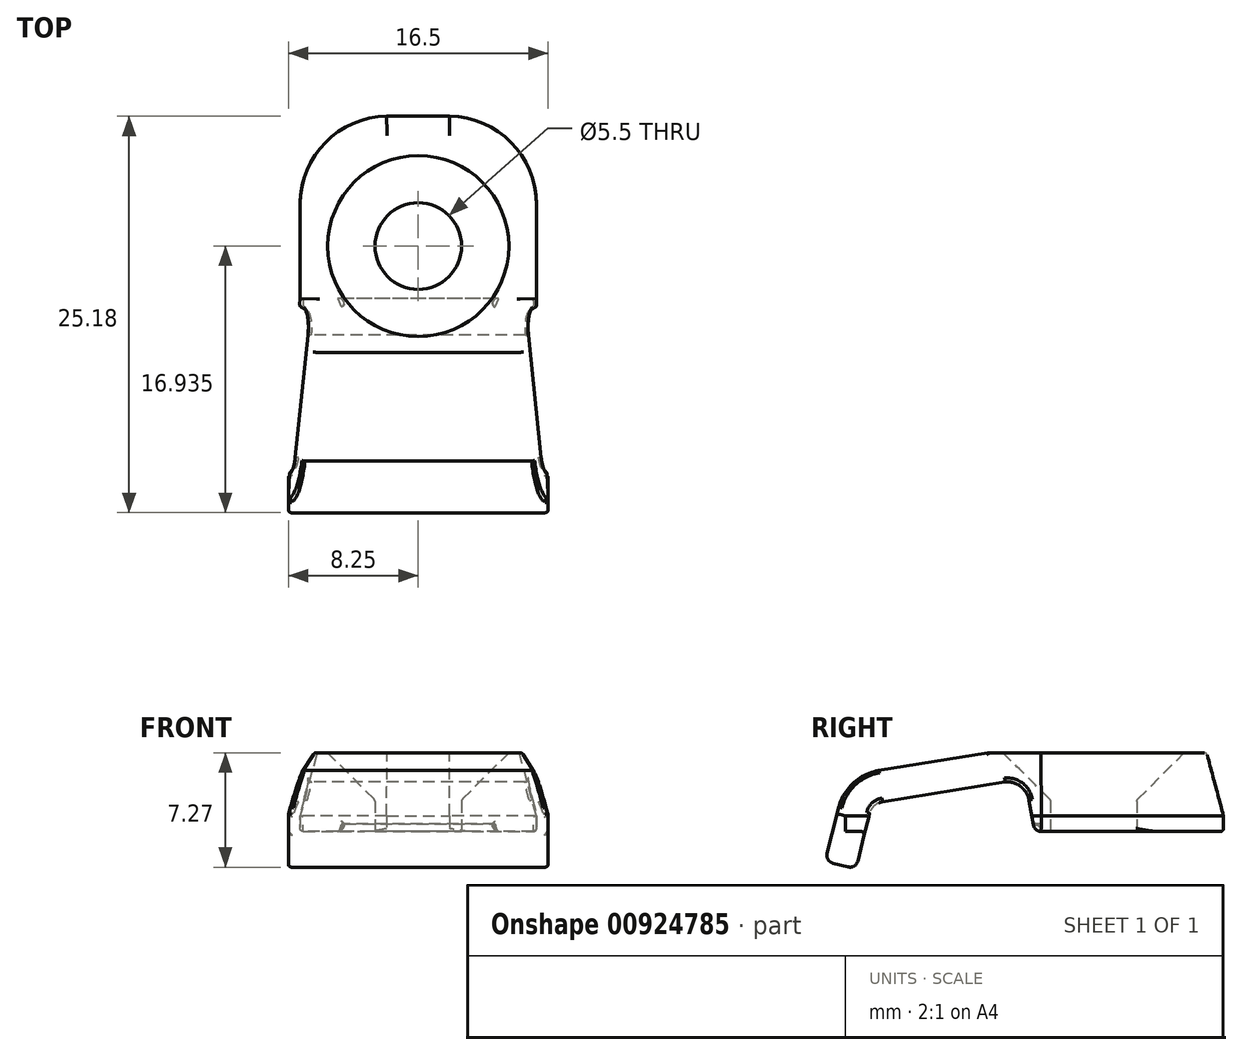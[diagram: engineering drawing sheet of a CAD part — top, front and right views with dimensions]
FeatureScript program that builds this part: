
annotation { "Feature Type Name" : "Feature", "Feature Type Description" : "" }
export const myFeature = defineFeature(function(context is Context, id is Id, definition is map)
    precondition{}
    {
        {
            var Q0;
            Q0=qCreatedBy(makeId("Right.planeOp"),FACE);
            var sketch = newSketch(context, id + "F0", { "sketchPlane" : qUnion([Q0])});
            skLineSegment(sketch, "E0", {"start": v(-8.94, -0.16) * mm, "end": v(-9.7, -3.19) * mm});
            skLineSegment(sketch, "E1", {"start": v(-10.3, -3.55) * mm, "end": v(-11.28, -3.3) * mm});
            skLineSegment(sketch, "E2", {"start": v(-11.64, -2.7) * mm, "end": v(-10.91, 0.2) * mm});
            skLineSegment(sketch, "E3", {"start": v(-8.37, 2.57) * mm, "end": v(-1.47, 3.7) * mm});
            skLineSegment(sketch, "E4", {"start": v(-1.47, 3.7) * mm, "end": v(13.53, 3.7) * mm});
            skLineSegment(sketch, "E5", {"start": v(13.53, 3.7) * mm, "end": v(13.53, -1.3) * mm});
            skLineSegment(sketch, "E6", {"start": v(1.95, -1.3) * mm, "end": v(13.53, -1.3) * mm});
            skLineSegment(sketch, "E7.0", {"start": v(-8.13, 0.58) * mm, "end": v(-0.36, 1.85) * mm});
            skArc(sketch, "E8", {"start": v(-8.37, 2.57) * mm, "mid": v(-10, 1.76) * mm, "end": v(-10.91, 0.2) * mm});
            skPoint(sketch, "E9.visualSharp", {"position": v(-8.78, 0.47) * mm});
            skArc(sketch, "E9.filletArc", {"start": v(-8.13, 0.58) * mm, "mid": v(-8.65, 0.33) * mm, "end": v(-8.94, -0.16) * mm});
            skPoint(sketch, "E10.visualSharp", {"position": v(-11.76, -3.19) * mm});
            skArc(sketch, "E10.filletArc", {"start": v(-11.64, -2.7) * mm, "mid": v(-11.58, -3.08) * mm, "end": v(-11.28, -3.3) * mm});
            skPoint(sketch, "E11.visualSharp", {"position": v(-9.82, -3.67) * mm});
            skArc(sketch, "E11.filletArc", {"start": v(-10.3, -3.55) * mm, "mid": v(-9.93, -3.5) * mm, "end": v(-9.7, -3.19) * mm});
            skLineSegment(sketch, "E12", {"start": v(1.46, -0.89) * mm, "end": v(1.19, 0.67) * mm});
            skArc(sketch, "E13", {"start": v(1.19, 0.67) * mm, "mid": v(0.65, 1.56) * mm, "end": v(-0.36, 1.85) * mm});
            skPoint(sketch, "E14.visualSharp", {"position": v(1.53, -1.3) * mm});
            skArc(sketch, "E14.filletArc", {"start": v(1.46, -0.89) * mm, "mid": v(1.63, -1.18) * mm, "end": v(1.95, -1.3) * mm});
            skSolve(sketch);
        }
        {
            var Q0;
            Q0=makeQuery(id+"F0.imprint","IMPRINT",FACE,{"disambiguationData":[TD([[makeQuery(id+"F0.imprint","IMPRINT",EDGE,{"derivedFrom":sQuery(id+"F0.wireOp",EDGE,"E0")}),-1.0]])]});
            extrude(context, id + "F1", {"entities" : qUnion([Q0]), "endBound" : BoundingType.SYMMETRIC, "depth" : 16.5 * mm, "offsetDistance" : 25 * mm});
        }
        {
            var Q0;
            Q0=makeQuery(id+"F1.opExtrude","SWEPT_FACE",FACE,{"disambiguationData":[OSD([sQuery(id+"F0.wireOp",EDGE,"E6")])]});
            var sketch = newSketch(context, id + "F2", { "sketchPlane" : qUnion([Q0])});
            skCircle(sketch, "E15", {"center": v(0, -5.28) * mm, "radius": 2.75 * mm});
            skLineSegment(sketch, "E16", {"start": v(0, 12.82) * mm, "end": v(0, -13.53) * mm, "construction": true});
            skPoint(sketch, "E17", {"position": v(7.5, -1.95) * mm});
            skPoint(sketch, "E18", {"position": v(-7.5, -1.95) * mm});
            skLineSegment(sketch, "E19", {"start": v(7.5, -1.95) * mm, "end": v(7.5, -7.95) * mm});
            skLineSegment(sketch, "E20", {"start": v(-7.5, -1.95) * mm, "end": v(-7.5, -7.95) * mm});
            skPoint(sketch, "E21", {"position": v(7.5, -7.95) * mm});
            skPoint(sketch, "E22", {"position": v(-7.5, -7.95) * mm});
            skPoint(sketch, "E23", {"position": v(-8.25, 10.47) * mm});
            skPoint(sketch, "E24", {"position": v(8.25, 10.47) * mm});
            skLineSegment(sketch, "E25", {"start": v(-7.5, -1.95) * mm, "end": v(-8.25, 10.47) * mm});
            skLineSegment(sketch, "E26", {"start": v(7.5, -1.95) * mm, "end": v(8.25, 10.47) * mm});
            skLineSegment(sketch, "E27", {"start": v(-8.25, 10.47) * mm, "end": v(-8.25, -1.95) * mm});
            skLineSegment(sketch, "E28", {"start": v(-8.25, -1.95) * mm, "end": v(-7.5, -1.95) * mm});
            skLineSegment(sketch, "E29", {"start": v(8.25, 10.47) * mm, "end": v(8.25, -1.95) * mm});
            skLineSegment(sketch, "E30", {"start": v(8.25, -1.95) * mm, "end": v(7.5, -1.95) * mm});
            skPoint(sketch, "E31", {"position": v(2, -13.53) * mm});
            skPoint(sketch, "E32", {"position": v(-2, -13.53) * mm});
            skArc(sketch, "E33", {"start": v(-7.5, -7.95) * mm, "mid": v(-5.9, -11.87) * mm, "end": v(-2, -13.53) * mm});
            skArc(sketch, "E34", {"start": v(2, -13.53) * mm, "mid": v(5.9, -11.87) * mm, "end": v(7.5, -7.95) * mm});
            skSolve(sketch);
        }
        {
            var Q0;
            {var subQ0=sQuery(id+"F2.wireOp",EDGE,"E27");Q0=makeQuery(id+"F2.imprint","IMPRINT",FACE,{"disambiguationData":[TD([[makeQuery(id+"F2.imprint","IMPRINT",EDGE,{"derivedFrom":subQ0}),1.0]])]});}
            var Q1;
            {var subQ0=sQuery(id+"F2.wireOp",EDGE,"E28");var subQ3=sQuery(id+"F2.wireOp",EDGE,"8BMvjW1E-92H8-ZigY-8C6n-Us3LmoF86cqy");var subQ4=makeQuery(id+"F2.imprint","INTERSECT",VERTEX,{"derivedFrom":[subQ0,subQ3]});Q1=makeQuery(id+"F2.imprint","IMPRINT",FACE,{"disambiguationData":[TD([[makeQuery(id+"F2.imprint","IMPRINT",EDGE,{"disambiguationData":[TD([[subQ4,-1.0]])],"derivedFrom":subQ3}),-1.0]])]});}
            var Q2;
            {var subQ0=sQuery(id+"F2.wireOp",EDGE,"8BMvjW1E-92H8-ZigY-8C6n-Us3LmoF86cqy");var subQ1=makeQuery(id+"F2.imprint","INTERSECT",VERTEX,{"derivedFrom":[sQuery(id+"F2.wireOp",EDGE,"E20"),subQ0]});Q2=makeQuery(id+"F2.imprint","IMPRINT",FACE,{"disambiguationData":[TD([[makeQuery(id+"F2.imprint","IMPRINT",EDGE,{"disambiguationData":[TD([[subQ1,1.0]])],"derivedFrom":subQ0}),-1.0]])]});}
            var Q3;
            {var subQ0=sQuery(id+"F2.wireOp",EDGE,"E20");Q3=makeQuery(id+"F2.imprint","IMPRINT",FACE,{"disambiguationData":[TD([[makeQuery(id+"F2.imprint","IMPRINT",EDGE,{"derivedFrom":subQ0}),-1.0]])]});}
            var Q4;
            {var subQ0=sQuery(id+"F2.wireOp",EDGE,"8BMvjW1E-92H8-ZigY-8C6n-Us3LmoF86cqy");var subQ1=makeQuery(id+"F2.imprint","INTERSECT",VERTEX,{"derivedFrom":[sQuery(id+"F2.wireOp",EDGE,"E19"),subQ0]});Q4=makeQuery(id+"F2.imprint","IMPRINT",FACE,{"disambiguationData":[TD([[makeQuery(id+"F2.imprint","IMPRINT",EDGE,{"disambiguationData":[TD([[subQ1,-1.0]])],"derivedFrom":subQ0}),-1.0]])]});}
            var Q5;
            {var subQ0=sQuery(id+"F2.wireOp",EDGE,"E19");Q5=makeQuery(id+"F2.imprint","IMPRINT",FACE,{"disambiguationData":[TD([[makeQuery(id+"F2.imprint","IMPRINT",EDGE,{"derivedFrom":subQ0}),1.0]])]});}
            var Q6;
            {var subQ0=sQuery(id+"F2.wireOp",EDGE,"E30");var subQ3=sQuery(id+"F2.wireOp",EDGE,"8BMvjW1E-92H8-ZigY-8C6n-Us3LmoF86cqy");var subQ4=makeQuery(id+"F2.imprint","INTERSECT",VERTEX,{"derivedFrom":[subQ0,subQ3]});Q6=makeQuery(id+"F2.imprint","IMPRINT",FACE,{"disambiguationData":[TD([[makeQuery(id+"F2.imprint","IMPRINT",EDGE,{"disambiguationData":[TD([[subQ4,1.0]])],"derivedFrom":subQ3}),-1.0]])]});}
            var Q7;
            {var subQ0=sQuery(id+"F2.wireOp",EDGE,"E29");Q7=makeQuery(id+"F2.imprint","IMPRINT",FACE,{"disambiguationData":[TD([[makeQuery(id+"F2.imprint","IMPRINT",EDGE,{"derivedFrom":subQ0}),-1.0]])]});}
            var Q8;
            Q8=makeQuery(id+"F2.imprint","IMPRINT",FACE,{"disambiguationData":[TD([[makeQuery(id+"F2.imprint","IMPRINT",EDGE,{"derivedFrom":sQuery(id+"F2.wireOp",EDGE,"E15")}),1.0]])]});
            extrude(context, id + "F3", {"entities" : qUnion([Q0, Q1, Q2, Q3, Q4, Q5, Q6, Q7, Q8]), "operationType" : NewBodyOperationType.REMOVE, "endBound" : BoundingType.THROUGH_ALL, "oppositeDirection" : true, "depth" : 25 * mm, "offsetDistance" : 25 * mm});
        }
        {
            var Q0;
            Q0=makeQuery(id+"F3.boolean.opBoolean","INTERSECT",EDGE,{"derivedFrom":[makeQuery(id+"F1.opExtrude","SWEPT_FACE",FACE,{"disambiguationData":[OSD([sQuery(id+"F0.wireOp",EDGE,"E4")])]}),makeQuery(id+"F3.opExtrude","SWEPT_FACE",FACE,{"disambiguationData":[OSD([sQuery(id+"F2.wireOp",EDGE,"E15")])]})]});
            chamfer(context, id + "F4", {"entities" : qUnion([Q0]), "width" : 3 * mm, "tangentPropagation" : true});
        }
        {
            var Q0;
            Q0=makeQuery(id+"F3.boolean.opBoolean","INTERSECT",EDGE,{"derivedFrom":[makeQuery(id+"F1.opExtrude","SWEPT_FACE",FACE,{"disambiguationData":[OSD([sQuery(id+"F0.wireOp",EDGE,"E4")])]}),makeQuery(id+"F3.opExtrude","SWEPT_FACE",FACE,{"disambiguationData":[OSD([sQuery(id+"F2.wireOp",EDGE,"E19")])]})]});
            var Q1;
            Q1=makeQuery(id+"F3.boolean.opBoolean","INTERSECT",EDGE,{"derivedFrom":[makeQuery(id+"F1.opExtrude","SWEPT_FACE",FACE,{"disambiguationData":[OSD([sQuery(id+"F0.wireOp",EDGE,"E4")])]}),makeQuery(id+"F3.opExtrude","SWEPT_FACE",FACE,{"disambiguationData":[OSD([sQuery(id+"F2.wireOp",EDGE,"E34")])]})]});
            var Q2;
            Q2=makeQuery(id+"F1.opExtrude","SWEPT_EDGE",EDGE,{"disambiguationData":[OSD([sQuery(id+"F0.wireOp",EDGE,"E4"),sQuery(id+"F0.wireOp",EDGE,"E5")])]});
            var Q3;
            Q3=makeQuery(id+"F3.boolean.opBoolean","INTERSECT",EDGE,{"derivedFrom":[makeQuery(id+"F1.opExtrude","SWEPT_FACE",FACE,{"disambiguationData":[OSD([sQuery(id+"F0.wireOp",EDGE,"E4")])]}),makeQuery(id+"F3.opExtrude","SWEPT_FACE",FACE,{"disambiguationData":[OSD([sQuery(id+"F2.wireOp",EDGE,"E33")])]})]});
            chamfer(context, id + "F5", {"entities" : qUnion([Q0, Q1, Q2, Q3]), "chamferType" : ChamferType.OFFSET_ANGLE, "width" : 4 * mm, "oppositeDirection" : false, "angle" : 15 * degree, "tangentPropagation" : true});
        }
        {
            var Q0;
            Q0=makeQuery(id+"F1.opExtrude","SWEPT_FACE",FACE,{"disambiguationData":[OSD([sQuery(id+"F0.wireOp",EDGE,"E6")])]});
            var sketch = newSketch(context, id + "F6", { "sketchPlane" : qUnion([Q0])});
            skCircle(sketch, "E35", {"center": v(0, -5.28) * mm, "radius": 5.9 * mm});
            skSolve(sketch);
        }
        {
            var Q0;
            Q0=makeQuery(id+"F6.imprint","IMPRINT",FACE,{"disambiguationData":[TD([[makeQuery(id+"F6.imprint","IMPRINT",EDGE,{"derivedFrom":makeQuery(id+"F3.boolean.opBoolean","COPY",EDGE,{"derivedFrom":makeQuery(id+"F3.opExtrude","CAP_EDGE",EDGE,{"disambiguationData":[OSD([sQuery(id+"F2.wireOp",EDGE,"E15")])],"isStart":true})})}),-1.0]])]});
            var Q1;
            {var subQ0=sQuery(id+"F6.wireOp",EDGE,"E35");var subQ1=makeQuery(id+"F1.opExtrude","SWEPT_EDGE",EDGE,{"disambiguationData":[OSD([sQuery(id+"F0.wireOp",EDGE,"E6"),sQuery(id+"F0.wireOp",EDGE,"E14.filletArc")])]});var subQ2=makeQuery(id+"F6.imprint","INTERSECT",VERTEX,{"disambiguationData":[OD(0.0)],"derivedFrom":[subQ1,subQ0]});Q1=makeQuery(id+"F6.imprint","IMPRINT",FACE,{"disambiguationData":[TD([[makeQuery(id+"F6.imprint","IMPRINT",EDGE,{"disambiguationData":[TD([[subQ2,-1.0]])],"derivedFrom":subQ0}),1.0]])]});}
            extrude(context, id + "F7", {"entities" : qUnion([Q0, Q1]), "operationType" : NewBodyOperationType.REMOVE, "oppositeDirection" : true, "depth" : 0.5 * mm, "offsetDistance" : 25 * mm});
        }
        {
            var Q0;
            Q0=makeQuery(id+"F5.opChamfer","BLEND_EDGE",EDGE,{"blendedFrom":[makeQuery(id+"F3.boolean.opBoolean","INTERSECT",EDGE,{"derivedFrom":[makeQuery(id+"F1.opExtrude","SWEPT_FACE",FACE,{"disambiguationData":[OSD([sQuery(id+"F0.wireOp",EDGE,"E4")])]}),makeQuery(id+"F3.opExtrude","SWEPT_FACE",FACE,{"disambiguationData":[OSD([sQuery(id+"F2.wireOp",EDGE,"E26")])]})]}),makeQuery(id+"F1.opExtrude","SWEPT_FACE",FACE,{"disambiguationData":[OSD([sQuery(id+"F0.wireOp",EDGE,"E3")])]})],"blendedInto":[makeQuery(id+"F1.opExtrude","SWEPT_FACE",FACE,{"disambiguationData":[OSD([sQuery(id+"F0.wireOp",EDGE,"E3")])]})]});
            var Q1;
            {var subQ0=makeQuery(id+"F1.opExtrude","SWEPT_FACE",FACE,{"disambiguationData":[OSD([sQuery(id+"F0.wireOp",EDGE,"E4")])]});Q1=makeQuery(id+"F5.opChamfer","BLEND_EDGE",EDGE,{"blendedFrom":[makeQuery(id+"F3.boolean.opBoolean","INTERSECT",EDGE,{"derivedFrom":[subQ0,makeQuery(id+"F3.opExtrude","SWEPT_FACE",FACE,{"disambiguationData":[OSD([sQuery(id+"F2.wireOp",EDGE,"E26")])]})]}),subQ0],"blendedInto":[subQ0]});}
            var Q2;
            {var subQ0=makeQuery(id+"F1.opExtrude","SWEPT_FACE",FACE,{"disambiguationData":[OSD([sQuery(id+"F0.wireOp",EDGE,"E4")])]});Q2=makeQuery(id+"F5.opChamfer","BLEND_EDGE",EDGE,{"blendedFrom":[makeQuery(id+"F3.boolean.opBoolean","INTERSECT",EDGE,{"derivedFrom":[subQ0,makeQuery(id+"F3.opExtrude","SWEPT_FACE",FACE,{"disambiguationData":[OSD([sQuery(id+"F2.wireOp",EDGE,"E19")])]})]}),subQ0],"blendedInto":[subQ0]});}
            var Q3;
            {var subQ0=makeQuery(id+"F1.opExtrude","SWEPT_FACE",FACE,{"disambiguationData":[OSD([sQuery(id+"F0.wireOp",EDGE,"E4")])]});Q3=makeQuery(id+"F5.opChamfer","BLEND_EDGE",EDGE,{"blendedFrom":[makeQuery(id+"F3.boolean.opBoolean","INTERSECT",EDGE,{"derivedFrom":[subQ0,makeQuery(id+"F3.opExtrude","SWEPT_FACE",FACE,{"disambiguationData":[OSD([sQuery(id+"F2.wireOp",EDGE,"E34")])]})]}),subQ0],"blendedInto":[subQ0]});}
            var Q4;
            {var subQ0=sQuery(id+"F0.wireOp",EDGE,"E4");Q4=makeQuery(id+"F5.opChamfer","BLEND_EDGE",EDGE,{"blendedFrom":[makeQuery(id+"F1.opExtrude","SWEPT_EDGE",EDGE,{"disambiguationData":[OSD([subQ0,sQuery(id+"F0.wireOp",EDGE,"E5")])]}),makeQuery(id+"F1.opExtrude","SWEPT_FACE",FACE,{"disambiguationData":[OSD([subQ0])]})],"blendedInto":[makeQuery(id+"F1.opExtrude","SWEPT_FACE",FACE,{"disambiguationData":[OSD([subQ0])]})]});}
            var Q5;
            {var subQ0=makeQuery(id+"F1.opExtrude","SWEPT_FACE",FACE,{"disambiguationData":[OSD([sQuery(id+"F0.wireOp",EDGE,"E4")])]});Q5=makeQuery(id+"F5.opChamfer","BLEND_EDGE",EDGE,{"blendedFrom":[makeQuery(id+"F3.boolean.opBoolean","INTERSECT",EDGE,{"derivedFrom":[subQ0,makeQuery(id+"F3.opExtrude","SWEPT_FACE",FACE,{"disambiguationData":[OSD([sQuery(id+"F2.wireOp",EDGE,"E33")])]})]}),subQ0],"blendedInto":[subQ0]});}
            var Q6;
            Q6=makeQuery(id+"F5.opChamfer","BLEND_EDGE",EDGE,{"blendedFrom":[makeQuery(id+"F3.boolean.opBoolean","INTERSECT",EDGE,{"derivedFrom":[makeQuery(id+"F1.opExtrude","SWEPT_FACE",FACE,{"disambiguationData":[OSD([sQuery(id+"F0.wireOp",EDGE,"E4")])]}),makeQuery(id+"F3.opExtrude","SWEPT_FACE",FACE,{"disambiguationData":[OSD([sQuery(id+"F2.wireOp",EDGE,"E25")])]})]}),makeQuery(id+"F1.opExtrude","SWEPT_FACE",FACE,{"disambiguationData":[OSD([sQuery(id+"F0.wireOp",EDGE,"E3")])]})],"blendedInto":[makeQuery(id+"F1.opExtrude","SWEPT_FACE",FACE,{"disambiguationData":[OSD([sQuery(id+"F0.wireOp",EDGE,"E3")])]})]});
            var Q7;
            {var subQ0=makeQuery(id+"F1.opExtrude","SWEPT_FACE",FACE,{"disambiguationData":[OSD([sQuery(id+"F0.wireOp",EDGE,"E4")])]});Q7=makeQuery(id+"F5.opChamfer","BLEND_EDGE",EDGE,{"blendedFrom":[makeQuery(id+"F3.boolean.opBoolean","INTERSECT",EDGE,{"derivedFrom":[subQ0,makeQuery(id+"F3.opExtrude","SWEPT_FACE",FACE,{"disambiguationData":[OSD([sQuery(id+"F2.wireOp",EDGE,"E25")])]})]}),subQ0],"blendedInto":[subQ0]});}
            var Q8;
            {var subQ0=makeQuery(id+"F1.opExtrude","SWEPT_FACE",FACE,{"disambiguationData":[OSD([sQuery(id+"F0.wireOp",EDGE,"E4")])]});Q8=makeQuery(id+"F5.opChamfer","BLEND_EDGE",EDGE,{"blendedFrom":[makeQuery(id+"F3.boolean.opBoolean","INTERSECT",EDGE,{"derivedFrom":[subQ0,makeQuery(id+"F3.opExtrude","SWEPT_FACE",FACE,{"disambiguationData":[OSD([sQuery(id+"F2.wireOp",EDGE,"E20")])]})]}),subQ0],"blendedInto":[subQ0]});}
            var Q9;
            Q9=makeQuery(id+"F5.opChamfer","BLEND_EDGE",EDGE,{"blendedFrom":[makeQuery(id+"F3.boolean.opBoolean","INTERSECT",EDGE,{"derivedFrom":[makeQuery(id+"F1.opExtrude","SWEPT_FACE",FACE,{"disambiguationData":[OSD([sQuery(id+"F0.wireOp",EDGE,"E4")])]}),makeQuery(id+"F3.opExtrude","SWEPT_FACE",FACE,{"disambiguationData":[OSD([sQuery(id+"F2.wireOp",EDGE,"E26")])]})]}),makeQuery(id+"F1.opExtrude","SWEPT_FACE",FACE,{"disambiguationData":[OSD([sQuery(id+"F0.wireOp",EDGE,"E8")])]})],"blendedInto":[makeQuery(id+"F1.opExtrude","SWEPT_FACE",FACE,{"disambiguationData":[OSD([sQuery(id+"F0.wireOp",EDGE,"E8")])]})]});
            var Q10;
            Q10=makeQuery(id+"F1.opExtrude","CAP_EDGE",EDGE,{"disambiguationData":[OSD([sQuery(id+"F0.wireOp",EDGE,"E2")])],"isStart":false});
            var Q11;
            Q11=makeQuery(id+"F5.opChamfer","BLEND_EDGE",EDGE,{"blendedFrom":[makeQuery(id+"F3.boolean.opBoolean","INTERSECT",EDGE,{"derivedFrom":[makeQuery(id+"F1.opExtrude","SWEPT_FACE",FACE,{"disambiguationData":[OSD([sQuery(id+"F0.wireOp",EDGE,"E4")])]}),makeQuery(id+"F3.opExtrude","SWEPT_FACE",FACE,{"disambiguationData":[OSD([sQuery(id+"F2.wireOp",EDGE,"E25")])]})]}),makeQuery(id+"F1.opExtrude","SWEPT_FACE",FACE,{"disambiguationData":[OSD([sQuery(id+"F0.wireOp",EDGE,"E8")])]})],"blendedInto":[makeQuery(id+"F1.opExtrude","SWEPT_FACE",FACE,{"disambiguationData":[OSD([sQuery(id+"F0.wireOp",EDGE,"E8")])]})]});
            var Q12;
            Q12=makeQuery(id+"F1.opExtrude","CAP_EDGE",EDGE,{"disambiguationData":[OSD([sQuery(id+"F0.wireOp",EDGE,"E2")])],"isStart":true});
            var Q13;
            Q13=makeQuery(id+"F5.opChamfer","BLEND_EDGE",EDGE,{"blendedFrom":[makeQuery(id+"F3.boolean.opBoolean","INTERSECT",EDGE,{"derivedFrom":[makeQuery(id+"F1.opExtrude","SWEPT_FACE",FACE,{"disambiguationData":[OSD([sQuery(id+"F0.wireOp",EDGE,"E4")])]}),makeQuery(id+"F3.opExtrude","SWEPT_FACE",FACE,{"disambiguationData":[OSD([sQuery(id+"F2.wireOp",EDGE,"E25")])]})]}),makeQuery(id+"F1.opExtrude","SWEPT_FACE",FACE,{"disambiguationData":[OSD([sQuery(id+"F0.wireOp",EDGE,"E7.0")])]})],"blendedInto":[makeQuery(id+"F1.opExtrude","SWEPT_FACE",FACE,{"disambiguationData":[OSD([sQuery(id+"F0.wireOp",EDGE,"E7.0")])]})]});
            var Q14;
            Q14=makeQuery(id+"F3.boolean.opBoolean","INTERSECT",EDGE,{"derivedFrom":[makeQuery(id+"F1.opExtrude","SWEPT_FACE",FACE,{"disambiguationData":[OSD([sQuery(id+"F0.wireOp",EDGE,"E12")])]}),makeQuery(id+"F3.opExtrude","SWEPT_FACE",FACE,{"disambiguationData":[OSD([sQuery(id+"F2.wireOp",EDGE,"E25")])]})]});
            var Q15;
            Q15=makeQuery(id+"F3.boolean.opBoolean","INTERSECT",EDGE,{"derivedFrom":[makeQuery(id+"F1.opExtrude","SWEPT_FACE",FACE,{"disambiguationData":[OSD([sQuery(id+"F0.wireOp",EDGE,"E14.filletArc")])]}),makeQuery(id+"F3.opExtrude","SWEPT_FACE",FACE,{"disambiguationData":[OSD([sQuery(id+"F2.wireOp",EDGE,"E25")])]})]});
            var Q16;
            Q16=makeQuery(id+"F3.boolean.opBoolean","COPY",EDGE,{"derivedFrom":makeQuery(id+"F3.opExtrude","CAP_EDGE",EDGE,{"disambiguationData":[OSD([sQuery(id+"F2.wireOp",EDGE,"E20")])],"isStart":true})});
            var Q17;
            Q17=makeQuery(id+"F7.boolean.opBoolean","INTERSECT",EDGE,{"derivedFrom":[makeQuery(id+"F1.opExtrude","SWEPT_FACE",FACE,{"disambiguationData":[OSD([sQuery(id+"F0.wireOp",EDGE,"E12")])]}),makeQuery(id+"F7.opExtrude","CAP_FACE",FACE,{"disambiguationData":[OSD([sQuery(id+"F2.wireOp",EDGE,"E15"),sQuery(id+"F6.wireOp",EDGE,"E35")])],"isStart":false})]});
            var Q18;
            Q18=makeQuery(id+"F1.opExtrude","CAP_EDGE",EDGE,{"disambiguationData":[OSD([sQuery(id+"F0.wireOp",EDGE,"E10.filletArc")])],"isStart":false});
            var Q19;
            Q19=makeQuery(id+"F1.opExtrude","CAP_EDGE",EDGE,{"disambiguationData":[OSD([sQuery(id+"F0.wireOp",EDGE,"E1")])],"isStart":false});
            var Q20;
            Q20=makeQuery(id+"F1.opExtrude","CAP_EDGE",EDGE,{"disambiguationData":[OSD([sQuery(id+"F0.wireOp",EDGE,"E11.filletArc")])],"isStart":false});
            var Q21;
            Q21=makeQuery(id+"F1.opExtrude","CAP_EDGE",EDGE,{"disambiguationData":[OSD([sQuery(id+"F0.wireOp",EDGE,"E0")])],"isStart":false});
            var Q22;
            Q22=makeQuery(id+"F3.boolean.opBoolean","INTERSECT",EDGE,{"derivedFrom":[makeQuery(id+"F1.opExtrude","SWEPT_FACE",FACE,{"disambiguationData":[OSD([sQuery(id+"F0.wireOp",EDGE,"E0")])]}),makeQuery(id+"F3.opExtrude","SWEPT_FACE",FACE,{"disambiguationData":[OSD([sQuery(id+"F2.wireOp",EDGE,"E26")])]})]});
            var Q23;
            Q23=makeQuery(id+"F5.opChamfer","BLEND_EDGE",EDGE,{"blendedFrom":[makeQuery(id+"F3.boolean.opBoolean","INTERSECT",EDGE,{"derivedFrom":[makeQuery(id+"F1.opExtrude","SWEPT_FACE",FACE,{"disambiguationData":[OSD([sQuery(id+"F0.wireOp",EDGE,"E4")])]}),makeQuery(id+"F3.opExtrude","SWEPT_FACE",FACE,{"disambiguationData":[OSD([sQuery(id+"F2.wireOp",EDGE,"E26")])]})]}),makeQuery(id+"F1.opExtrude","SWEPT_FACE",FACE,{"disambiguationData":[OSD([sQuery(id+"F0.wireOp",EDGE,"E9.filletArc")])]})],"blendedInto":[makeQuery(id+"F1.opExtrude","SWEPT_FACE",FACE,{"disambiguationData":[OSD([sQuery(id+"F0.wireOp",EDGE,"E9.filletArc")])]})]});
            var Q24;
            Q24=makeQuery(id+"F5.opChamfer","BLEND_EDGE",EDGE,{"blendedFrom":[makeQuery(id+"F3.boolean.opBoolean","INTERSECT",EDGE,{"derivedFrom":[makeQuery(id+"F1.opExtrude","SWEPT_FACE",FACE,{"disambiguationData":[OSD([sQuery(id+"F0.wireOp",EDGE,"E4")])]}),makeQuery(id+"F3.opExtrude","SWEPT_FACE",FACE,{"disambiguationData":[OSD([sQuery(id+"F2.wireOp",EDGE,"E26")])]})]}),makeQuery(id+"F1.opExtrude","SWEPT_FACE",FACE,{"disambiguationData":[OSD([sQuery(id+"F0.wireOp",EDGE,"E0")])]})],"blendedInto":[makeQuery(id+"F1.opExtrude","SWEPT_FACE",FACE,{"disambiguationData":[OSD([sQuery(id+"F0.wireOp",EDGE,"E0")])]})]});
            var Q25;
            Q25=makeQuery(id+"F5.opChamfer","BLEND_EDGE",EDGE,{"blendedFrom":[makeQuery(id+"F3.boolean.opBoolean","INTERSECT",EDGE,{"derivedFrom":[makeQuery(id+"F1.opExtrude","SWEPT_FACE",FACE,{"disambiguationData":[OSD([sQuery(id+"F0.wireOp",EDGE,"E4")])]}),makeQuery(id+"F3.opExtrude","SWEPT_FACE",FACE,{"disambiguationData":[OSD([sQuery(id+"F2.wireOp",EDGE,"E26")])]})]}),makeQuery(id+"F1.opExtrude","SWEPT_FACE",FACE,{"disambiguationData":[OSD([sQuery(id+"F0.wireOp",EDGE,"E7.0")])]})],"blendedInto":[makeQuery(id+"F1.opExtrude","SWEPT_FACE",FACE,{"disambiguationData":[OSD([sQuery(id+"F0.wireOp",EDGE,"E7.0")])]})]});
            var Q26;
            Q26=makeQuery(id+"F5.opChamfer","BLEND_EDGE",EDGE,{"blendedFrom":[makeQuery(id+"F3.boolean.opBoolean","INTERSECT",EDGE,{"derivedFrom":[makeQuery(id+"F1.opExtrude","SWEPT_FACE",FACE,{"disambiguationData":[OSD([sQuery(id+"F0.wireOp",EDGE,"E4")])]}),makeQuery(id+"F3.opExtrude","SWEPT_FACE",FACE,{"disambiguationData":[OSD([sQuery(id+"F2.wireOp",EDGE,"E26")])]})]}),makeQuery(id+"F1.opExtrude","SWEPT_FACE",FACE,{"disambiguationData":[OSD([sQuery(id+"F0.wireOp",EDGE,"E13")])]})],"blendedInto":[makeQuery(id+"F1.opExtrude","SWEPT_FACE",FACE,{"disambiguationData":[OSD([sQuery(id+"F0.wireOp",EDGE,"E13")])]})]});
            var Q27;
            Q27=makeQuery(id+"F3.boolean.opBoolean","INTERSECT",EDGE,{"derivedFrom":[makeQuery(id+"F1.opExtrude","SWEPT_FACE",FACE,{"disambiguationData":[OSD([sQuery(id+"F0.wireOp",EDGE,"E12")])]}),makeQuery(id+"F3.opExtrude","SWEPT_FACE",FACE,{"disambiguationData":[OSD([sQuery(id+"F2.wireOp",EDGE,"E26")])]})]});
            var Q28;
            Q28=makeQuery(id+"F5.opChamfer","BLEND_EDGE",EDGE,{"blendedFrom":[makeQuery(id+"F3.boolean.opBoolean","INTERSECT",EDGE,{"derivedFrom":[makeQuery(id+"F1.opExtrude","SWEPT_FACE",FACE,{"disambiguationData":[OSD([sQuery(id+"F0.wireOp",EDGE,"E4")])]}),makeQuery(id+"F3.opExtrude","SWEPT_FACE",FACE,{"disambiguationData":[OSD([sQuery(id+"F2.wireOp",EDGE,"E26")])]})]}),makeQuery(id+"F1.opExtrude","SWEPT_FACE",FACE,{"disambiguationData":[OSD([sQuery(id+"F0.wireOp",EDGE,"E12")])]})],"blendedInto":[makeQuery(id+"F1.opExtrude","SWEPT_FACE",FACE,{"disambiguationData":[OSD([sQuery(id+"F0.wireOp",EDGE,"E12")])]})]});
            var Q29;
            Q29=makeQuery(id+"F3.boolean.opBoolean","COPY",EDGE,{"derivedFrom":makeQuery(id+"F3.opExtrude","CAP_EDGE",EDGE,{"disambiguationData":[OSD([sQuery(id+"F2.wireOp",EDGE,"E19")])],"isStart":true})});
            var Q30;
            Q30=makeQuery(id+"F3.boolean.opBoolean","INTERSECT",EDGE,{"derivedFrom":[makeQuery(id+"F1.opExtrude","SWEPT_FACE",FACE,{"disambiguationData":[OSD([sQuery(id+"F0.wireOp",EDGE,"E14.filletArc")])]}),makeQuery(id+"F3.opExtrude","SWEPT_FACE",FACE,{"disambiguationData":[OSD([sQuery(id+"F2.wireOp",EDGE,"E26")])]})]});
            var Q31;
            Q31=makeQuery(id+"F3.boolean.opBoolean","COPY",EDGE,{"derivedFrom":makeQuery(id+"F3.opExtrude","CAP_EDGE",EDGE,{"disambiguationData":[OSD([sQuery(id+"F2.wireOp",EDGE,"E34")])],"isStart":true})});
            var Q32;
            Q32=makeQuery(id+"F1.opExtrude","SWEPT_EDGE",EDGE,{"disambiguationData":[OSD([sQuery(id+"F0.wireOp",EDGE,"E5"),sQuery(id+"F0.wireOp",EDGE,"E6")])]});
            var Q33;
            Q33=makeQuery(id+"F3.boolean.opBoolean","COPY",EDGE,{"derivedFrom":makeQuery(id+"F3.opExtrude","CAP_EDGE",EDGE,{"disambiguationData":[OSD([sQuery(id+"F2.wireOp",EDGE,"E33")])],"isStart":true})});
            var Q34;
            Q34=makeQuery(id+"F7.boolean.opBoolean","COPY",EDGE,{"derivedFrom":makeQuery(id+"F7.opExtrude","CAP_EDGE",EDGE,{"disambiguationData":[OSD([sQuery(id+"F6.wireOp",EDGE,"E35")])],"isStart":true})});
            var Q35;
            Q35=makeQuery(id+"F7.boolean.opBoolean","INTERSECT",EDGE,{"disambiguationData":[OD(1.0)],"derivedFrom":[makeQuery(id+"F1.opExtrude","SWEPT_FACE",FACE,{"disambiguationData":[OSD([sQuery(id+"F0.wireOp",EDGE,"E14.filletArc")])]}),makeQuery(id+"F7.opExtrude","SWEPT_FACE",FACE,{"disambiguationData":[OSD([sQuery(id+"F6.wireOp",EDGE,"E35")])]})]});
            var Q36;
            Q36=makeQuery(id+"F7.boolean.opBoolean","INTERSECT",EDGE,{"disambiguationData":[OD(0.0)],"derivedFrom":[makeQuery(id+"F1.opExtrude","SWEPT_FACE",FACE,{"disambiguationData":[OSD([sQuery(id+"F0.wireOp",EDGE,"E14.filletArc")])]}),makeQuery(id+"F7.opExtrude","SWEPT_FACE",FACE,{"disambiguationData":[OSD([sQuery(id+"F6.wireOp",EDGE,"E35")])]})]});
            var Q37;
            Q37=makeQuery(id+"F7.boolean.opBoolean","COPY",EDGE,{"derivedFrom":makeQuery(id+"F7.opExtrude","CAP_EDGE",EDGE,{"disambiguationData":[OSD([sQuery(id+"F2.wireOp",EDGE,"E15")])],"isStart":false})});
            var Q38;
            {var subQ0=makeQuery(id+"F3.opExtrude","SWEPT_FACE",FACE,{"disambiguationData":[OSD([sQuery(id+"F2.wireOp",EDGE,"E15")])]});Q38=makeQuery(id+"F4.opChamfer","BLEND_EDGE",EDGE,{"blendedFrom":[makeQuery(id+"F3.boolean.opBoolean","INTERSECT",EDGE,{"derivedFrom":[makeQuery(id+"F1.opExtrude","SWEPT_FACE",FACE,{"disambiguationData":[OSD([sQuery(id+"F0.wireOp",EDGE,"E4")])]}),subQ0]}),makeQuery(id+"F3.boolean.opBoolean","COPY",FACE,{"derivedFrom":subQ0})],"blendedInto":[makeQuery(id+"F3.boolean.opBoolean","COPY",FACE,{"derivedFrom":subQ0})]});}
            var Q39;
            Q39=makeQuery(id+"F5.opChamfer","BLEND_EDGE",EDGE,{"blendedFrom":[makeQuery(id+"F3.boolean.opBoolean","INTERSECT",EDGE,{"derivedFrom":[makeQuery(id+"F1.opExtrude","SWEPT_FACE",FACE,{"disambiguationData":[OSD([sQuery(id+"F0.wireOp",EDGE,"E4")])]}),makeQuery(id+"F3.opExtrude","SWEPT_FACE",FACE,{"disambiguationData":[OSD([sQuery(id+"F2.wireOp",EDGE,"E25")])]})]}),makeQuery(id+"F1.opExtrude","SWEPT_FACE",FACE,{"disambiguationData":[OSD([sQuery(id+"F0.wireOp",EDGE,"E13")])]})],"blendedInto":[makeQuery(id+"F1.opExtrude","SWEPT_FACE",FACE,{"disambiguationData":[OSD([sQuery(id+"F0.wireOp",EDGE,"E13")])]})]});
            var Q40;
            Q40=makeQuery(id+"F5.opChamfer","BLEND_EDGE",EDGE,{"blendedFrom":[makeQuery(id+"F3.boolean.opBoolean","INTERSECT",EDGE,{"derivedFrom":[makeQuery(id+"F1.opExtrude","SWEPT_FACE",FACE,{"disambiguationData":[OSD([sQuery(id+"F0.wireOp",EDGE,"E4")])]}),makeQuery(id+"F3.opExtrude","SWEPT_FACE",FACE,{"disambiguationData":[OSD([sQuery(id+"F2.wireOp",EDGE,"E25")])]})]}),makeQuery(id+"F1.opExtrude","SWEPT_FACE",FACE,{"disambiguationData":[OSD([sQuery(id+"F0.wireOp",EDGE,"E12")])]})],"blendedInto":[makeQuery(id+"F1.opExtrude","SWEPT_FACE",FACE,{"disambiguationData":[OSD([sQuery(id+"F0.wireOp",EDGE,"E12")])]})]});
            var Q41;
            Q41=makeQuery(id+"F5.opChamfer","BLEND_EDGE",EDGE,{"blendedFrom":[makeQuery(id+"F3.boolean.opBoolean","INTERSECT",EDGE,{"derivedFrom":[makeQuery(id+"F1.opExtrude","SWEPT_FACE",FACE,{"disambiguationData":[OSD([sQuery(id+"F0.wireOp",EDGE,"E4")])]}),makeQuery(id+"F3.opExtrude","SWEPT_FACE",FACE,{"disambiguationData":[OSD([sQuery(id+"F2.wireOp",EDGE,"E25")])]})]}),makeQuery(id+"F1.opExtrude","SWEPT_FACE",FACE,{"disambiguationData":[OSD([sQuery(id+"F0.wireOp",EDGE,"E9.filletArc")])]})],"blendedInto":[makeQuery(id+"F1.opExtrude","SWEPT_FACE",FACE,{"disambiguationData":[OSD([sQuery(id+"F0.wireOp",EDGE,"E9.filletArc")])]})]});
            var Q42;
            Q42=makeQuery(id+"F3.boolean.opBoolean","INTERSECT",EDGE,{"derivedFrom":[makeQuery(id+"F1.opExtrude","SWEPT_FACE",FACE,{"disambiguationData":[OSD([sQuery(id+"F0.wireOp",EDGE,"E0")])]}),makeQuery(id+"F3.opExtrude","SWEPT_FACE",FACE,{"disambiguationData":[OSD([sQuery(id+"F2.wireOp",EDGE,"E25")])]})]});
            var Q43;
            Q43=makeQuery(id+"F5.opChamfer","BLEND_EDGE",EDGE,{"blendedFrom":[makeQuery(id+"F3.boolean.opBoolean","INTERSECT",EDGE,{"derivedFrom":[makeQuery(id+"F1.opExtrude","SWEPT_FACE",FACE,{"disambiguationData":[OSD([sQuery(id+"F0.wireOp",EDGE,"E4")])]}),makeQuery(id+"F3.opExtrude","SWEPT_FACE",FACE,{"disambiguationData":[OSD([sQuery(id+"F2.wireOp",EDGE,"E25")])]})]}),makeQuery(id+"F1.opExtrude","SWEPT_FACE",FACE,{"disambiguationData":[OSD([sQuery(id+"F0.wireOp",EDGE,"E0")])]})],"blendedInto":[makeQuery(id+"F1.opExtrude","SWEPT_FACE",FACE,{"disambiguationData":[OSD([sQuery(id+"F0.wireOp",EDGE,"E0")])]})]});
            var Q44;
            Q44=makeQuery(id+"F1.opExtrude","CAP_EDGE",EDGE,{"disambiguationData":[OSD([sQuery(id+"F0.wireOp",EDGE,"E11.filletArc")])],"isStart":true});
            var Q45;
            Q45=makeQuery(id+"F1.opExtrude","CAP_EDGE",EDGE,{"disambiguationData":[OSD([sQuery(id+"F0.wireOp",EDGE,"E1")])],"isStart":true});
            var Q46;
            Q46=makeQuery(id+"F1.opExtrude","CAP_EDGE",EDGE,{"disambiguationData":[OSD([sQuery(id+"F0.wireOp",EDGE,"E10.filletArc")])],"isStart":true});
            var Q47;
            Q47=makeQuery(id+"F5.opChamfer","BLEND_EDGE",EDGE,{"blendedFrom":[makeQuery(id+"F3.boolean.opBoolean","INTERSECT",EDGE,{"derivedFrom":[makeQuery(id+"F1.opExtrude","SWEPT_FACE",FACE,{"disambiguationData":[OSD([sQuery(id+"F0.wireOp",EDGE,"E4")])]}),makeQuery(id+"F3.opExtrude","SWEPT_FACE",FACE,{"disambiguationData":[OSD([sQuery(id+"F2.wireOp",EDGE,"E25")])]})]}),makeQuery(id+"F1.opExtrude","SWEPT_FACE",FACE,{"disambiguationData":[OSD([sQuery(id+"F0.wireOp",EDGE,"E2")])]})],"blendedInto":[makeQuery(id+"F1.opExtrude","SWEPT_FACE",FACE,{"disambiguationData":[OSD([sQuery(id+"F0.wireOp",EDGE,"E2")])]})]});
            var Q48;
            Q48=makeQuery(id+"F5.opChamfer","BLEND_EDGE",EDGE,{"blendedFrom":[makeQuery(id+"F3.boolean.opBoolean","INTERSECT",EDGE,{"derivedFrom":[makeQuery(id+"F1.opExtrude","SWEPT_FACE",FACE,{"disambiguationData":[OSD([sQuery(id+"F0.wireOp",EDGE,"E4")])]}),makeQuery(id+"F3.opExtrude","SWEPT_FACE",FACE,{"disambiguationData":[OSD([sQuery(id+"F2.wireOp",EDGE,"E26")])]})]}),makeQuery(id+"F1.opExtrude","SWEPT_FACE",FACE,{"disambiguationData":[OSD([sQuery(id+"F0.wireOp",EDGE,"E2")])]})],"blendedInto":[makeQuery(id+"F1.opExtrude","SWEPT_FACE",FACE,{"disambiguationData":[OSD([sQuery(id+"F0.wireOp",EDGE,"E2")])]})]});
            var Q49;
            Q49=makeQuery(id+"F7.boolean.opBoolean","INTERSECT",EDGE,{"disambiguationData":[OD(0.0)],"derivedFrom":[makeQuery(id+"F1.opExtrude","SWEPT_FACE",FACE,{"disambiguationData":[OSD([sQuery(id+"F0.wireOp",EDGE,"E12")])]}),makeQuery(id+"F7.opExtrude","SWEPT_FACE",FACE,{"disambiguationData":[OSD([sQuery(id+"F6.wireOp",EDGE,"E35")])]})]});
            var Q50;
            Q50=makeQuery(id+"F7.boolean.opBoolean","INTERSECT",EDGE,{"disambiguationData":[OD(1.0)],"derivedFrom":[makeQuery(id+"F1.opExtrude","SWEPT_FACE",FACE,{"disambiguationData":[OSD([sQuery(id+"F0.wireOp",EDGE,"E12")])]}),makeQuery(id+"F7.opExtrude","SWEPT_FACE",FACE,{"disambiguationData":[OSD([sQuery(id+"F6.wireOp",EDGE,"E35")])]})]});
            var Q51;
            Q51=makeQuery(id+"F1.opExtrude","CAP_EDGE",EDGE,{"disambiguationData":[OSD([sQuery(id+"F0.wireOp",EDGE,"E0")])],"isStart":true});
            var Q52;
            Q52=makeQuery(id+"F3.boolean.opBoolean","INTERSECT",EDGE,{"derivedFrom":[makeQuery(id+"F1.opExtrude","SWEPT_FACE",FACE,{"disambiguationData":[OSD([sQuery(id+"F0.wireOp",EDGE,"E0")])]}),makeQuery(id+"F3.opExtrude","CAP_FACE",FACE,{"disambiguationData":[OSD([sQuery(id+"F0.wireOp",EDGE,"E5"),sQuery(id+"F0.wireOp",EDGE,"E6"),sQuery(id+"F2.wireOp",EDGE,"E19"),sQuery(id+"F2.wireOp",EDGE,"E26"),sQuery(id+"F2.wireOp",EDGE,"E29"),sQuery(id+"F2.wireOp",EDGE,"E34")])],"isStart":true})]});
            var Q53;
            Q53=makeQuery(id+"F3.boolean.opBoolean","INTERSECT",EDGE,{"derivedFrom":[makeQuery(id+"F1.opExtrude","SWEPT_FACE",FACE,{"disambiguationData":[OSD([sQuery(id+"F0.wireOp",EDGE,"E0")])]}),makeQuery(id+"F3.opExtrude","CAP_FACE",FACE,{"disambiguationData":[OSD([sQuery(id+"F0.wireOp",EDGE,"E5"),sQuery(id+"F0.wireOp",EDGE,"E6"),sQuery(id+"F2.wireOp",EDGE,"E20"),sQuery(id+"F2.wireOp",EDGE,"E25"),sQuery(id+"F2.wireOp",EDGE,"E27"),sQuery(id+"F2.wireOp",EDGE,"E33")])],"isStart":true})]});
            fillet(context, id + "F8", {"entities" : qUnion([Q0, Q1, Q2, Q3, Q4, Q5, Q6, Q7, Q8, Q9, Q10, Q11, Q12, Q13, Q14, Q15, Q16, Q17, Q18, Q19, Q20, Q21, Q22, Q23, Q24, Q25, Q26, Q27, Q28, Q29, Q30, Q31, Q32, Q33, Q34, Q35, Q36, Q37, Q38, Q39, Q40, Q41, Q42, Q43, Q44, Q45, Q46, Q47, Q48, Q49, Q50, Q51, Q52, Q53]), "radius" : 0.2 * mm, "tangentPropagation" : true, "allowEdgeOverflow" : false});
        }
    });
